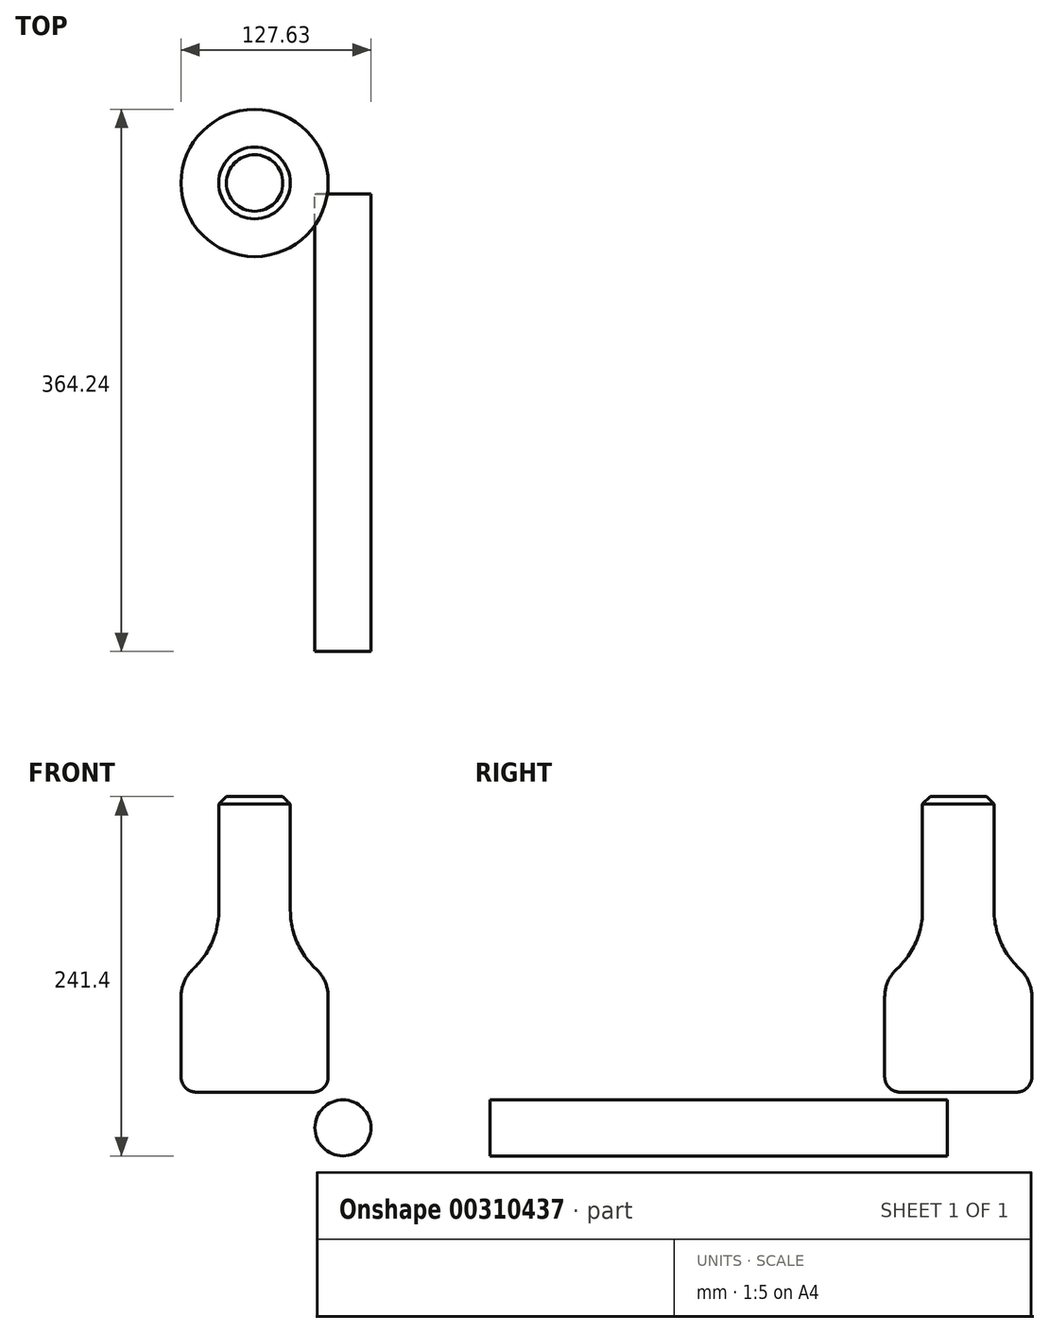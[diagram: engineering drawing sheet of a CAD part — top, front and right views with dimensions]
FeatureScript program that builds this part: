
annotation { "Feature Type Name" : "Feature", "Feature Type Description" : "" }
export const myFeature = defineFeature(function(context is Context, id is Id, definition is map)
    precondition{}
    {
        {
            var Q0;
            Q0=qCreatedBy(makeId("Top.planeOp"),FACE);
            var sketch = newSketch(context, id + "F0", { "sketchPlane" : qUnion([Q0])});
            skCircle(sketch, "E0", {"center": v(0, 7.36) * mm, "radius": 49.46 * mm});
            skSolve(sketch);
        }
        {
            var Q0;
            Q0 = qSketchRegion(id + "F0", true);
            extrude(context, id + "F1", {"entities" : qUnion([Q0]), "depth" : 100 * mm});
        }
        {
            var Q0;
            Q0=makeQuery(id+"F1.opExtrude","CAP_EDGE",EDGE,{"disambiguationData":[OSD([sQuery(id+"F0.wireOp",EDGE,"E0")])],"isStart":false});
            chamfer(context, id + "F2", {"entities" : qUnion([Q0]), "width" : 25.4 * mm, "tangentPropagation" : true});
        }
        {
            var Q0;
            {var subQ0=sQuery(id+"F0.wireOp",EDGE,"E0");Q0=makeQuery(id+"F2.opChamfer","BLEND_EDGE",EDGE,{"blendedFrom":[makeQuery(id+"F1.opExtrude","CAP_EDGE",EDGE,{"disambiguationData":[OSD([subQ0])],"isStart":false}),makeQuery(id+"F1.opExtrude","SWEPT_FACE",FACE,{"disambiguationData":[OSD([subQ0])]})],"blendedInto":[makeQuery(id+"F1.opExtrude","SWEPT_FACE",FACE,{"disambiguationData":[OSD([subQ0])]})]});}
            fillet(context, id + "F3", {"entities" : qUnion([Q0]), "radius" : 25.56 * mm, "tangentPropagation" : true, "allowEdgeOverflow" : false});
        }
        {
            var Q0;
            Q0=makeQuery(id+"F1.opExtrude","CAP_FACE",FACE,{"disambiguationData":[OSD([sQuery(id+"F0.wireOp",EDGE,"E0")])],"isStart":false});
            extrude(context, id + "F4", {"entities" : qUnion([Q0]), "operationType" : NewBodyOperationType.ADD, "depth" : 98.52 * mm});
        }
        {
            var Q0;
            {var subQ0=sQuery(id+"F0.wireOp",EDGE,"E0");Q0=makeQuery(id+"F4.boolean.opBoolean","MERGE",EDGE,{"derivedFrom":[makeQuery(id+"F2.opChamfer","BLEND_EDGE",EDGE,{"blendedFrom":[makeQuery(id+"F1.opExtrude","CAP_EDGE",EDGE,{"disambiguationData":[OSD([subQ0])],"isStart":false}),makeQuery(id+"F1.opExtrude","CAP_FACE",FACE,{"disambiguationData":[OSD([subQ0])],"isStart":false})],"blendedInto":[makeQuery(id+"F1.opExtrude","CAP_FACE",FACE,{"disambiguationData":[OSD([subQ0])],"isStart":false})]}),makeQuery(id+"F4.opExtrude","CAP_EDGE",EDGE,{"disambiguationData":[OSD([subQ0])],"isStart":true})]});}
            fillet(context, id + "F5", {"entities" : qUnion([Q0]), "radius" : 53 * mm, "tangentPropagation" : true, "allowEdgeOverflow" : false});
        }
        {
            var Q0;
            Q0=makeQuery(id+"F4.opExtrude","CAP_FACE",FACE,{"disambiguationData":[OSD([sQuery(id+"F0.wireOp",EDGE,"E0")])],"isStart":false});
            chamfer(context, id + "F6", {"entities" : qUnion([Q0]), "width" : 5.08 * mm, "tangentPropagation" : true});
        }
        {
            var Q0;
            Q0=makeQuery(id+"F1.opExtrude","CAP_EDGE",EDGE,{"disambiguationData":[OSD([sQuery(id+"F0.wireOp",EDGE,"E0")])],"isStart":true});
            fillet(context, id + "F7", {"entities" : qUnion([Q0]), "radius" : 10.16 * mm, "tangentPropagation" : true, "allowEdgeOverflow" : false});
        }
        {
            var Q0;
            Q0=qCreatedBy(makeId("Front.planeOp"),FACE);
            var sketch = newSketch(context, id + "F8", { "sketchPlane" : qUnion([Q0])});
            skCircle(sketch, "E1", {"center": v(59.35, -24.05) * mm, "radius": 18.82 * mm});
            skSolve(sketch);
        }
        {
            var Q0;
            Q0 = qSketchRegion(id + "F8", true);
            extrude(context, id + "F9", {"entities" : qUnion([Q0]), "depth" : 307.42 * mm});
        }
    });
